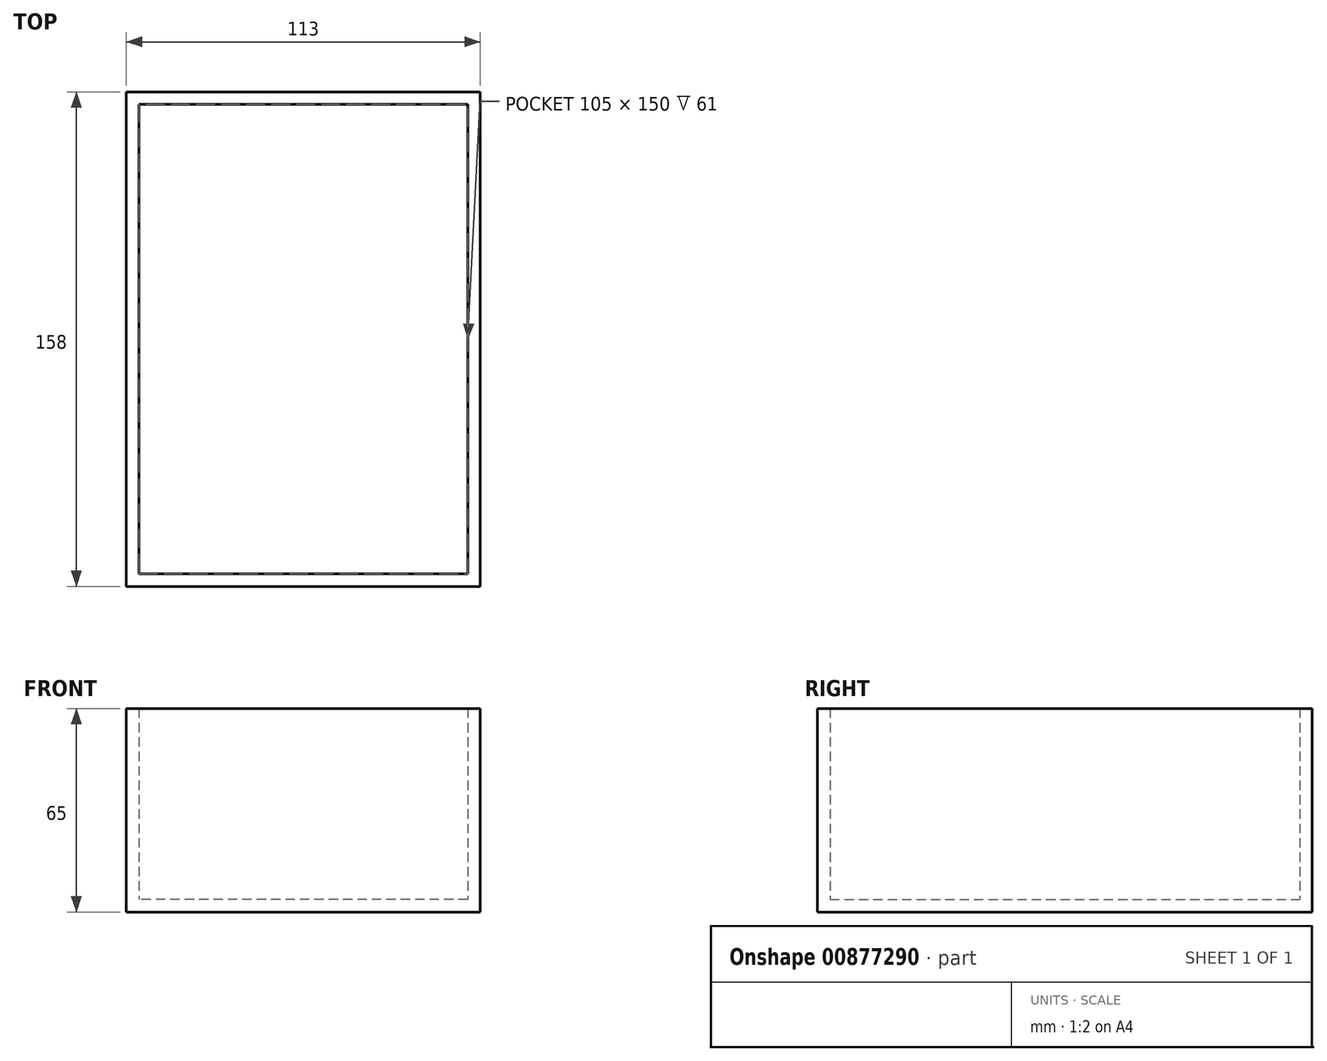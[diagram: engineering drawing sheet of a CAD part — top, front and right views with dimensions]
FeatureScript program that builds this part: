
annotation { "Feature Type Name" : "Feature", "Feature Type Description" : "" }
export const myFeature = defineFeature(function(context is Context, id is Id, definition is map)
    precondition{}
    {
        {
            var Q0;
            Q0=qCreatedBy(makeId("Top.planeOp"),FACE);
            var sketch = newSketch(context, id + "F0", { "sketchPlane" : qUnion([Q0])});
            skPoint(sketch, "E0.middle", {"position": v(0, 0) * mm});
            skLineSegment(sketch, "E1.bottom", {"start": v(52.5, -75) * mm, "end": v(-52.5, -75) * mm});
            skLineSegment(sketch, "E1.top", {"start": v(52.5, 75) * mm, "end": v(-52.5, 75) * mm});
            skLineSegment(sketch, "E1.left", {"start": v(52.5, -75) * mm, "end": v(52.5, 75) * mm});
            skLineSegment(sketch, "E1.right", {"start": v(-52.5, -75) * mm, "end": v(-52.5, 75) * mm});
            skLineSegment(sketch, "E2.bottom", {"start": v(56.5, -79) * mm, "end": v(-56.5, -79) * mm});
            skLineSegment(sketch, "E2.top", {"start": v(56.5, 79) * mm, "end": v(-56.5, 79) * mm});
            skLineSegment(sketch, "E2.left", {"start": v(56.5, -79) * mm, "end": v(56.5, 79) * mm});
            skLineSegment(sketch, "E2.right", {"start": v(-56.5, -79) * mm, "end": v(-56.5, 79) * mm});
            skSolve(sketch);
        }
        {
            var Q0;
            Q0=makeQuery(id+"F0.imprint","IMPRINT",FACE,{"disambiguationData":[TD([[makeQuery(id+"F0.imprint","IMPRINT",EDGE,{"derivedFrom":sQuery(id+"F0.wireOp",EDGE,"E1.bottom")}),1.0]])]});
            extrude(context, id + "F1", {"entities" : qUnion([Q0]), "depth" : 65 * mm, "offsetDistance" : 25.4 * mm});
        }
        {
            var Q0;
            Q0=makeQuery(id+"F0.imprint","IMPRINT",FACE,{"disambiguationData":[TD([[makeQuery(id+"F0.imprint","IMPRINT",EDGE,{"derivedFrom":sQuery(id+"F0.wireOp",EDGE,"E1.bottom")}),-1.0]])]});
            extrude(context, id + "F2", {"entities" : qUnion([Q0]), "operationType" : NewBodyOperationType.ADD, "depth" : 4 * mm, "offsetDistance" : 25.4 * mm});
        }
    });
